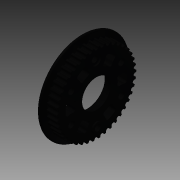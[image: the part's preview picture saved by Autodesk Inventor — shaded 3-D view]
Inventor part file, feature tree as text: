
AUTODESK INVENTOR PART (.ipt)
format: ipt  version: 2014 SP1 (Build 180222100, 222)  size: 1,481,216 bytes
history: native  units: in
note: dims shown in document units (in); Inventor stores cm internally (conversion verified against a paired STEP export)
features: other x2, sketch x1, imported_body x1
ambient origin geometry x8: Origin, YZ Plane, XZ Plane, XY Plane, X Axis, Y Axis, Z Axis, Center Point
bodies: Body1 (feature_tree)
feature tree (4):
  other  "42 tooth HTD Pulley half"
  other  "42 tooth HTD Pulley half1"
  sketch  "Sketch2"
  imported_body  "Base1"
